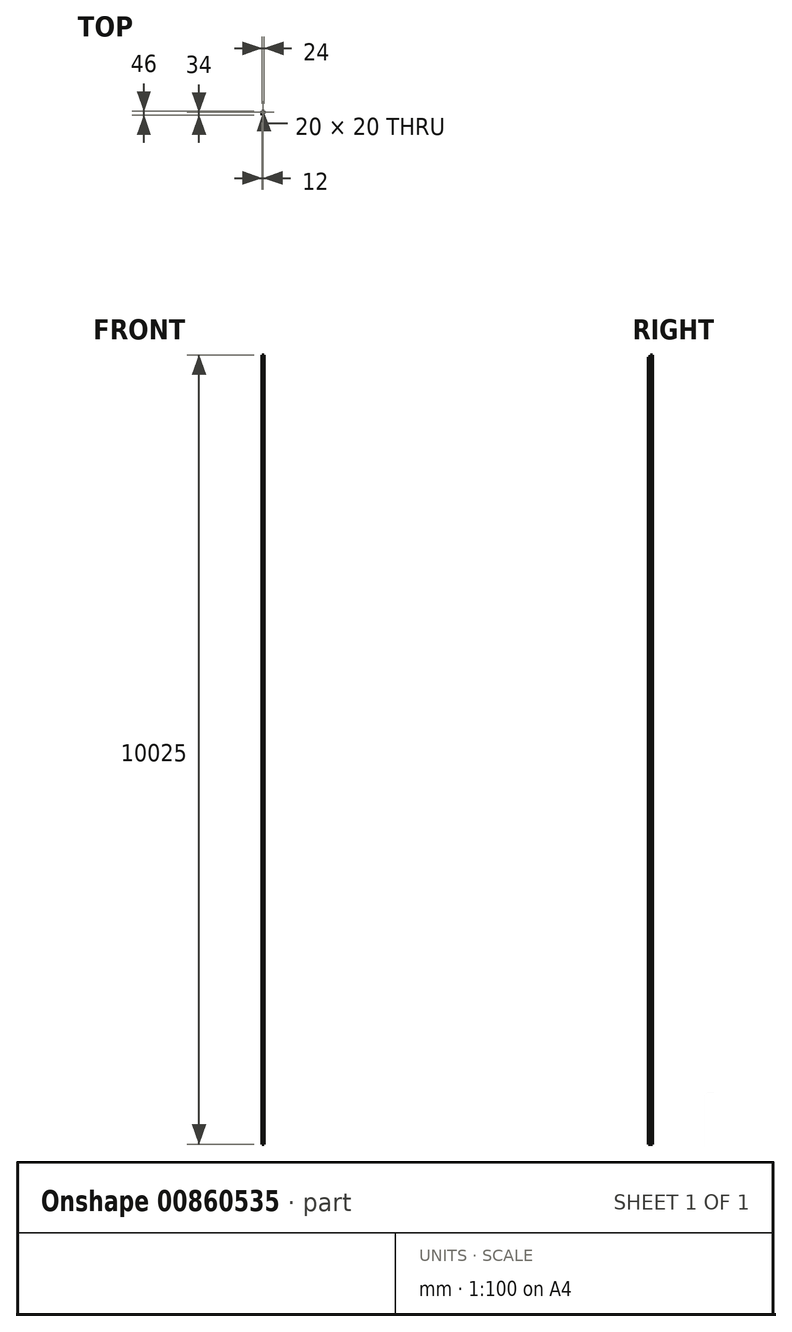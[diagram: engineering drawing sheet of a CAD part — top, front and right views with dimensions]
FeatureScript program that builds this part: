
annotation { "Feature Type Name" : "Feature", "Feature Type Description" : "" }
export const myFeature = defineFeature(function(context is Context, id is Id, definition is map)
    precondition{}
    {
        {
            var Q0;
            Q0=qCreatedBy(makeId("Top.planeOp"),FACE);
            var sketch = newSketch(context, id + "F0", { "sketchPlane" : qUnion([Q0])});
            skLineSegment(sketch, "E0.bottom", {"start": v(-12, 12) * mm, "end": v(12, 12) * mm});
            skLineSegment(sketch, "E0.top", {"start": v(-12, -12) * mm, "end": v(12, -12) * mm});
            skLineSegment(sketch, "E0.left", {"start": v(-12, 12) * mm, "end": v(-12, -12) * mm});
            skLineSegment(sketch, "E0.right", {"start": v(12, 12) * mm, "end": v(12, -12) * mm});
            skPoint(sketch, "E0.middle", {"position": v(0, 0) * mm});
            skSolve(sketch);
        }
        {
            var Q0;
            Q0=makeQuery(id+"F0.imprint","IMPRINT",FACE,{"disambiguationData":[TD([[makeQuery(id+"F0.imprint","IMPRINT",EDGE,{"derivedFrom":sQuery(id+"F0.wireOp",EDGE,"E0.bottom")}),-1.0]])]});
            extrude(context, id + "F1", {"entities" : qUnion([Q0]), "depth" : 10000 * mm, "offsetDistance" : 25 * mm});
        }
        {
            var Q0;
            Q0=makeQuery(id+"F1.opExtrude","CAP_FACE",FACE,{"disambiguationData":[OSD([sQuery(id+"F0.wireOp",EDGE,"E0.bottom"),sQuery(id+"F0.wireOp",EDGE,"E0.top"),sQuery(id+"F0.wireOp",EDGE,"E0.left"),sQuery(id+"F0.wireOp",EDGE,"E0.right")])],"isStart":false});
            extrude(context, id + "F2", {"entities" : qUnion([Q0]), "operationType" : NewBodyOperationType.ADD, "depth" : 25 * mm, "offsetDistance" : 25 * mm});
        }
        {
            var Q0;
            Q0=makeQuery(id+"F2.opExtrude","CAP_FACE",FACE,{"disambiguationData":[OSD([sQuery(id+"F0.wireOp",EDGE,"E0.bottom"),sQuery(id+"F0.wireOp",EDGE,"E0.top"),sQuery(id+"F0.wireOp",EDGE,"E0.left"),sQuery(id+"F0.wireOp",EDGE,"E0.right")])],"isStart":false});
            var Q1;
            Q1=makeQuery(id+"F1.opExtrude","CAP_FACE",FACE,{"disambiguationData":[OSD([sQuery(id+"F0.wireOp",EDGE,"E0.bottom"),sQuery(id+"F0.wireOp",EDGE,"E0.top"),sQuery(id+"F0.wireOp",EDGE,"E0.left"),sQuery(id+"F0.wireOp",EDGE,"E0.right")])],"isStart":true});
            shell(context, id + "F3", {"entities" : qUnion([Q0, Q1]), "thickness" : 2 * mm});
        }
        {
            var Q0;
            Q0=qCreatedBy(makeId("Top.planeOp"),FACE);
            var sketch = newSketch(context, id + "F4", { "sketchPlane" : qUnion([Q0])});
            skLineSegment(sketch, "E1.bottom", {"start": v(-12, -12) * mm, "end": v(-10, -12) * mm});
            skLineSegment(sketch, "E1.top", {"start": v(-12, -34) * mm, "end": v(-10, -34) * mm});
            skLineSegment(sketch, "E1.left", {"start": v(-12, -12) * mm, "end": v(-12, -34) * mm});
            skLineSegment(sketch, "E1.right", {"start": v(-10, -12) * mm, "end": v(-10, -34) * mm});
            skLineSegment(sketch, "E2.0", {"start": v(-12, -12) * mm, "end": v(12, -12) * mm, "construction": true});
            skSolve(sketch);
        }
        {
            var Q0;
            Q0=makeQuery(id+"F4.imprint","IMPRINT",FACE,{"disambiguationData":[TD([[makeQuery(id+"F4.imprint","IMPRINT",EDGE,{"derivedFrom":sQuery(id+"F4.wireOp",EDGE,"E1.bottom")}),-1.0]])]});
            extrude(context, id + "F5", {"entities" : qUnion([Q0]), "operationType" : NewBodyOperationType.ADD, "depth" : 10000 * mm, "offsetDistance" : 25 * mm});
        }
    });
